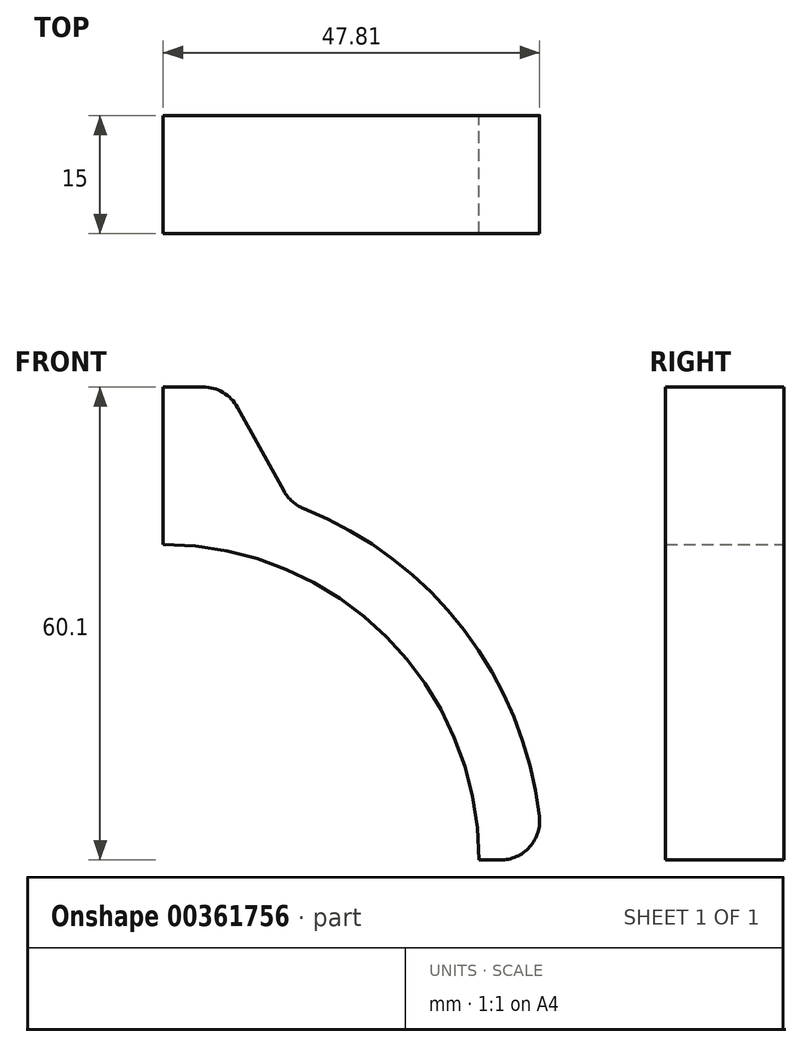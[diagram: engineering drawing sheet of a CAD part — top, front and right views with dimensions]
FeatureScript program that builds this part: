
annotation { "Feature Type Name" : "Feature", "Feature Type Description" : "" }
export const myFeature = defineFeature(function(context is Context, id is Id, definition is map)
    precondition{}
    {
        {
            var Q0;
            Q0=qCreatedBy(makeId("Front.planeOp"),FACE);
            var sketch = newSketch(context, id + "F0", { "sketchPlane" : qUnion([Q0])});
            skArc(sketch, "E0", {"start": v(40.1, 0) * mm, "mid": v(28.35, 28.35) * mm, "end": v(0, 40.1) * mm});
            skLineSegment(sketch, "E1", {"start": v(0, 40.1) * mm, "end": v(0, 60.1) * mm});
            skArc(sketch, "E2.0", {"start": v(47.78, 5.58) * mm, "mid": v(38.19, 29.25) * mm, "end": v(17.84, 44.67) * mm});
            skLineSegment(sketch, "E3", {"start": v(40.1, 0) * mm, "end": v(42.8, 0) * mm});
            skLineSegment(sketch, "E4", {"start": v(0, 60.1) * mm, "end": v(5.05, 60.1) * mm});
            skLineSegment(sketch, "E5", {"start": v(9.43, 57.52) * mm, "end": v(15.32, 46.89) * mm});
            skPoint(sketch, "E6.visualSharp", {"position": v(16.2, 45.29) * mm});
            skArc(sketch, "E6.filletArc", {"start": v(15.32, 46.89) * mm, "mid": v(16.39, 45.56) * mm, "end": v(17.84, 44.67) * mm});
            skPoint(sketch, "E7.visualSharp", {"position": v(8, 60.1) * mm});
            skArc(sketch, "E7.filletArc", {"start": v(9.43, 57.52) * mm, "mid": v(7.6, 59.4) * mm, "end": v(5.05, 60.1) * mm});
            skPoint(sketch, "E8.visualSharp", {"position": v(48.1, 0) * mm});
            skArc(sketch, "E8.filletArc", {"start": v(42.8, 0) * mm, "mid": v(46.54, 1.68) * mm, "end": v(47.78, 5.58) * mm});
            skSolve(sketch);
        }
        {
            var Q0;
            Q0=makeQuery(id+"F0.imprint","IMPRINT",FACE,{"disambiguationData":[TD([[makeQuery(id+"F0.imprint","IMPRINT",EDGE,{"derivedFrom":sQuery(id+"F0.wireOp",EDGE,"E0")}),-1.0]])]});
            extrude(context, id + "F1", {"entities" : qUnion([Q0]), "depth" : 15 * mm, "offsetDistance" : 25 * mm});
        }
        {
            var Q0;
            Q0=qCreatedBy(makeId("Front.planeOp"),FACE);
            cPlane(context, id + "F2", {"entities" : qUnion([Q0]), "cplaneType" : CPlaneType.OFFSET, "offset" : 7.5 * mm, "width" : 150 * mm, "height" : 150 * mm});
        }
    });
